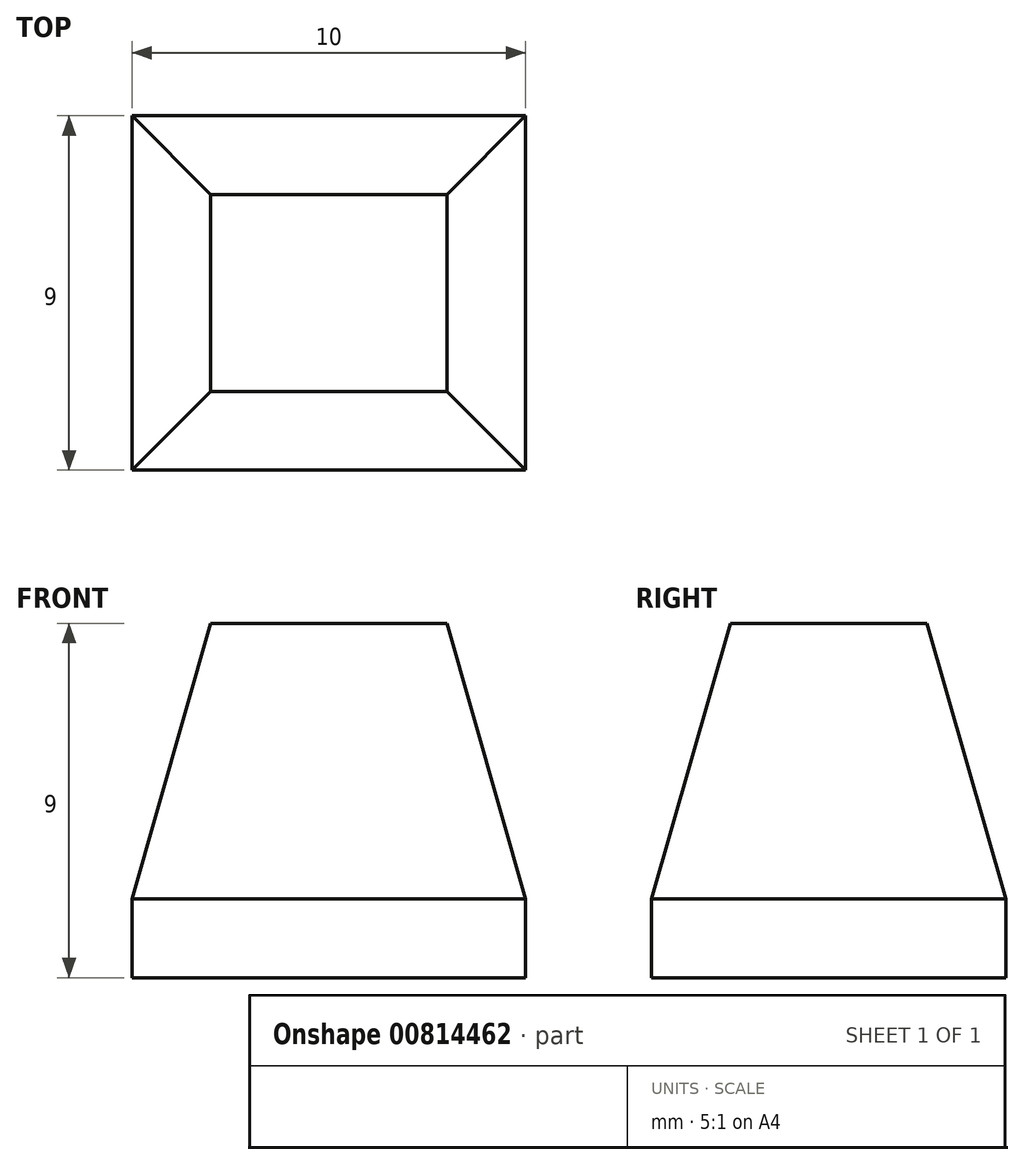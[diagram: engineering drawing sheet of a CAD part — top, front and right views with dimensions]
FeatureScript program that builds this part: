
annotation { "Feature Type Name" : "Feature", "Feature Type Description" : "" }
export const myFeature = defineFeature(function(context is Context, id is Id, definition is map)
    precondition{}
    {
        {
            var Q0;
            Q0=qCreatedBy(makeId("Right.planeOp"),FACE);
            var sketch = newSketch(context, id + "F0", { "sketchPlane" : qUnion([Q0])});
            skLineSegment(sketch, "E0.bottom", {"start": v(0, 0) * mm, "end": v(9, 0) * mm});
            skLineSegment(sketch, "E0.top", {"start": v(0, 9) * mm, "end": v(9, 9) * mm});
            skLineSegment(sketch, "E0.left", {"start": v(0, 0) * mm, "end": v(0, 9) * mm});
            skLineSegment(sketch, "E0.right", {"start": v(9, 0) * mm, "end": v(9, 9) * mm});
            skLineSegment(sketch, "E1", {"start": v(0, 2) * mm, "end": v(2, 9) * mm});
            skLineSegment(sketch, "E2", {"start": v(7, 9) * mm, "end": v(9, 2) * mm});
            skSolve(sketch);
        }
        {
            var Q0;
            {var subQ1=sQuery(id+"F0.wireOp",EDGE,"E0.bottom");Q0=makeQuery(id+"F0.imprint","IMPRINT",FACE,{"disambiguationData":[TD([[makeQuery(id+"F0.imprint","IMPRINT",EDGE,{"derivedFrom":subQ1}),1.0]])]});}
            extrude(context, id + "F1", {"entities" : qUnion([Q0]), "depth" : 10 * mm, "offsetDistance" : 25 * mm});
        }
        {
            var Q0;
            Q0=makeQuery(id+"F1.opExtrude","SWEPT_FACE",FACE,{"disambiguationData":[OSD([sQuery(id+"F0.wireOp",EDGE,"E0.left")])]});
            var sketch = newSketch(context, id + "F2", { "sketchPlane" : qUnion([Q0])});
            skLineSegment(sketch, "E3.0.0", {"start": v(0, 2) * mm, "end": v(0, 0) * mm});
            skLineSegment(sketch, "E3.0.1", {"start": v(0, 0) * mm, "end": v(10, 0) * mm});
            skLineSegment(sketch, "E3.0.2", {"start": v(10, 0) * mm, "end": v(10, 2) * mm});
            skLineSegment(sketch, "E3.0.3", {"start": v(10, 2) * mm, "end": v(0, 2) * mm});
            skLineSegment(sketch, "E4.0.0", {"start": v(0, 9) * mm, "end": v(0, 2) * mm});
            skLineSegment(sketch, "E4.0.1", {"start": v(0, 2) * mm, "end": v(10, 2) * mm});
            skLineSegment(sketch, "E4.0.2", {"start": v(10, 2) * mm, "end": v(10, 9) * mm});
            skLineSegment(sketch, "E4.0.3", {"start": v(10, 9) * mm, "end": v(0, 9) * mm});
            skLineSegment(sketch, "E5", {"start": v(10, 2) * mm, "end": v(8, 9) * mm});
            skLineSegment(sketch, "E6", {"start": v(0, 2) * mm, "end": v(2, 9) * mm});
            skLineSegment(sketch, "E7.bottom", {"start": v(4, 9) * mm, "end": v(6, 9) * mm});
            skLineSegment(sketch, "E7.top", {"start": v(4, 6) * mm, "end": v(6, 6) * mm});
            skLineSegment(sketch, "E7.left", {"start": v(4, 9) * mm, "end": v(4, 6) * mm});
            skLineSegment(sketch, "E7.right", {"start": v(6, 9) * mm, "end": v(6, 6) * mm});
            skSolve(sketch);
        }
        {
            var Q0;
            {var subQ0=sQuery(id+"F2.wireOp",EDGE,"E4.0.2");Q0=makeQuery(id+"F2.imprint","IMPRINT",FACE,{"disambiguationData":[TD([[makeQuery(id+"F2.imprint","IMPRINT",EDGE,{"derivedFrom":subQ0}),1.0]])]});}
            var Q1;
            Q1=makeQuery(id+"F2.imprint","IMPRINT",FACE,{"disambiguationData":[TD([[makeQuery(id+"F2.imprint","IMPRINT",EDGE,{"derivedFrom":sQuery(id+"F2.wireOp",EDGE,"E7.bottom")}),-1.0]])]});
            var Q2;
            {var subQ0=sQuery(id+"F2.wireOp",EDGE,"E4.0.0");Q2=makeQuery(id+"F2.imprint","IMPRINT",FACE,{"disambiguationData":[TD([[makeQuery(id+"F2.imprint","IMPRINT",EDGE,{"derivedFrom":subQ0}),1.0]])]});}
            extrude(context, id + "F3", {"entities" : qUnion([Q0, Q1, Q2]), "operationType" : NewBodyOperationType.REMOVE, "endBound" : BoundingType.THROUGH_ALL, "oppositeDirection" : true, "depth" : 25 * mm, "offsetDistance" : 25 * mm});
        }
    });
